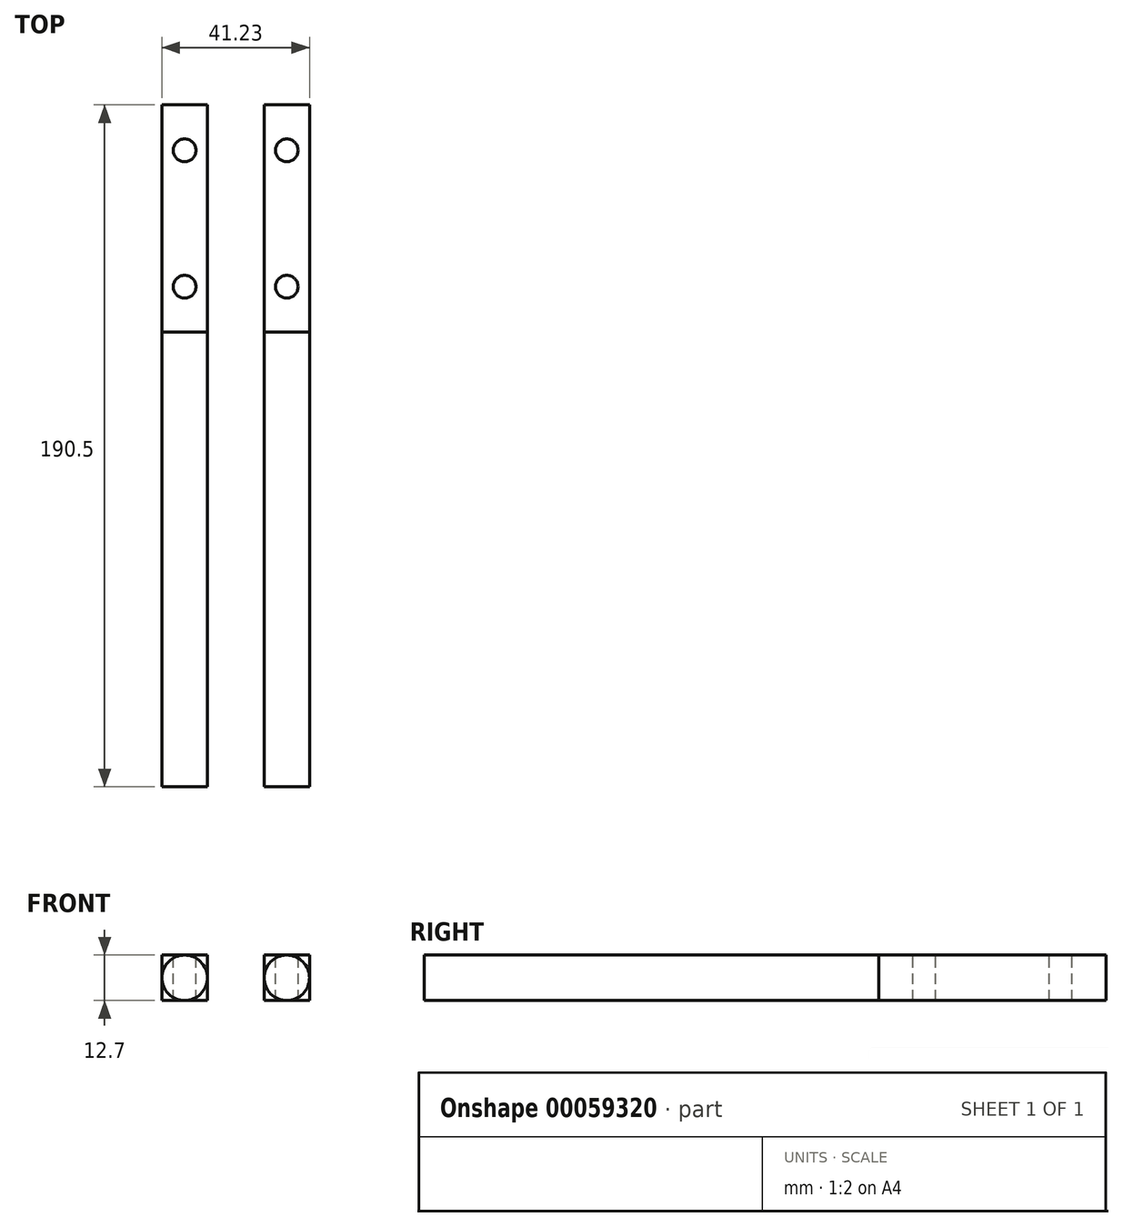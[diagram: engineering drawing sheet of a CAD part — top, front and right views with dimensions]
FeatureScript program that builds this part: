
annotation { "Feature Type Name" : "Feature", "Feature Type Description" : "" }
export const myFeature = defineFeature(function(context is Context, id is Id, definition is map)
    precondition{}
    {
        {
            var Q0;
            Q0=qCreatedBy(makeId("Front.planeOp"),FACE);
            var sketch = newSketch(context, id + "F0", { "sketchPlane" : qUnion([Q0])});
            skCircle(sketch, "E0", {"center": v(0, 0) * mm, "radius": 6.35 * mm});
            skSolve(sketch);
        }
        {
            var Q0;
            Q0 = qSketchRegion(id + "F0", true);
            extrude(context, id + "F1", {"entities" : qUnion([Q0]), "depth" : 127 * mm});
        }
        {
            var Q0;
            Q0=qCreatedBy(makeId("Front.planeOp"),FACE);
            var sketch = newSketch(context, id + "F2", { "sketchPlane" : qUnion([Q0])});
            skLineSegment(sketch, "E1.bottom", {"start": v(-6.35, 6.35) * mm, "end": v(6.35, 6.35) * mm});
            skLineSegment(sketch, "E1.top", {"start": v(-6.35, -6.35) * mm, "end": v(6.35, -6.35) * mm});
            skLineSegment(sketch, "E1.left", {"start": v(-6.35, 6.35) * mm, "end": v(-6.35, -6.35) * mm});
            skLineSegment(sketch, "E1.right", {"start": v(6.35, 6.35) * mm, "end": v(6.35, -6.35) * mm});
            skSolve(sketch);
        }
        {
            var Q0;
            Q0 = qSketchRegion(id + "F2", true);
            extrude(context, id + "F3", {"entities" : qUnion([Q0]), "operationType" : NewBodyOperationType.ADD, "oppositeDirection" : true, "depth" : 63.5 * mm});
        }
        {
            var Q0;
            Q0=makeQuery(id+"F3.opExtrude","SWEPT_FACE",FACE,{"disambiguationData":[OSD([sQuery(id+"F2.wireOp",EDGE,"E1.bottom")])]});
            var sketch = newSketch(context, id + "F4", { "sketchPlane" : qUnion([Q0])});
            skCircle(sketch, "E2", {"center": v(0, 12.7) * mm, "radius": 3.18 * mm});
            skCircle(sketch, "E3", {"center": v(0, 50.8) * mm, "radius": 3.18 * mm});
            skSolve(sketch);
        }
        {
            var Q0;
            Q0 = qSketchRegion(id + "F4", true);
            extrude(context, id + "F5", {"entities" : qUnion([Q0]), "operationType" : NewBodyOperationType.REMOVE, "oppositeDirection" : true, "depth" : 254 * mm});
        }
        {
            var Q0;
            Q0=qCreatedBy(makeId("Front.planeOp"),FACE);
            var sketch = newSketch(context, id + "F6", { "sketchPlane" : qUnion([Q0])});
            skCircle(sketch, "E4", {"center": v(28.53, 0) * mm, "radius": 6.35 * mm});
            skSolve(sketch);
        }
        {
            var Q0;
            Q0 = qSketchRegion(id + "F6", true);
            extrude(context, id + "F7", {"entities" : qUnion([Q0]), "depth" : 127 * mm});
        }
        {
            var Q0;
            Q0=qCreatedBy(makeId("Front.planeOp"),FACE);
            var sketch = newSketch(context, id + "F8", { "sketchPlane" : qUnion([Q0])});
            skLineSegment(sketch, "E5.bottom", {"start": v(22.18, 6.35) * mm, "end": v(34.88, 6.35) * mm});
            skLineSegment(sketch, "E5.top", {"start": v(22.18, -6.35) * mm, "end": v(34.88, -6.35) * mm});
            skLineSegment(sketch, "E5.left", {"start": v(22.18, 6.35) * mm, "end": v(22.18, -6.35) * mm});
            skLineSegment(sketch, "E5.right", {"start": v(34.88, 6.35) * mm, "end": v(34.88, -6.35) * mm});
            skSolve(sketch);
        }
        {
            var Q0;
            Q0 = qSketchRegion(id + "F8", true);
            extrude(context, id + "F9", {"entities" : qUnion([Q0]), "operationType" : NewBodyOperationType.ADD, "oppositeDirection" : true, "depth" : 63.5 * mm});
        }
        {
            var Q0;
            Q0=makeQuery(id+"F9.opExtrude","SWEPT_FACE",FACE,{"disambiguationData":[OSD([sQuery(id+"F8.wireOp",EDGE,"E5.bottom")])]});
            var sketch = newSketch(context, id + "F10", { "sketchPlane" : qUnion([Q0])});
            skCircle(sketch, "E6", {"center": v(28.53, 50.8) * mm, "radius": 3.18 * mm});
            skCircle(sketch, "E7", {"center": v(28.53, 12.7) * mm, "radius": 3.17 * mm});
            skSolve(sketch);
        }
        {
            var Q0;
            Q0 = qSketchRegion(id + "F10", true);
            extrude(context, id + "F11", {"entities" : qUnion([Q0]), "operationType" : NewBodyOperationType.REMOVE, "oppositeDirection" : true, "depth" : 254 * mm});
        }
    });
